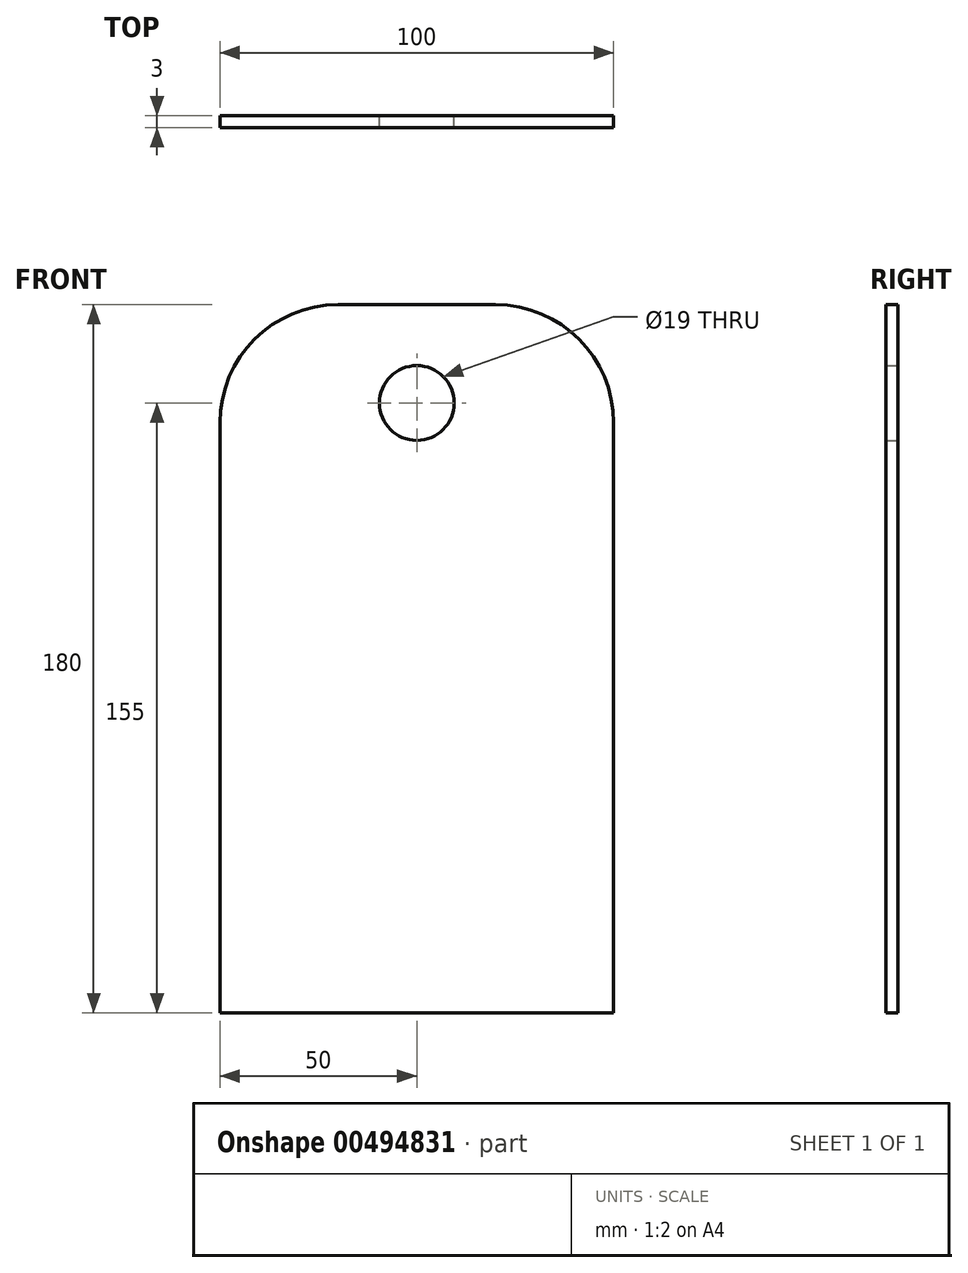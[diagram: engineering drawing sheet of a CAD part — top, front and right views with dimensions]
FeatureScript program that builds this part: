
annotation { "Feature Type Name" : "Feature", "Feature Type Description" : "" }
export const myFeature = defineFeature(function(context is Context, id is Id, definition is map)
    precondition{}
    {
        {
            var Q0;
            Q0=qCreatedBy(makeId("Front.planeOp"),FACE);
            var sketch = newSketch(context, id + "F0", { "sketchPlane" : qUnion([Q0])});
            skLineSegment(sketch, "E0.bottom", {"start": v(50, -90) * mm, "end": v(-50, -90) * mm});
            skLineSegment(sketch, "E0.top", {"start": v(50, 90) * mm, "end": v(-50, 90) * mm});
            skLineSegment(sketch, "E0.left", {"start": v(50, -90) * mm, "end": v(50, 90) * mm});
            skLineSegment(sketch, "E0.right", {"start": v(-50, -90) * mm, "end": v(-50, 90) * mm});
            skPoint(sketch, "E0.middle", {"position": v(0, 0) * mm});
            skCircle(sketch, "E1", {"center": v(0, 65) * mm, "radius": 9.5 * mm});
            skSolve(sketch);
        }
        {
            var Q0;
            Q0 = qSketchRegion(id + "F0", true);
            extrude(context, id + "F1", {"entities" : qUnion([Q0]), "depth" : 3 * mm});
        }
        {
            var Q0;
            Q0=makeQuery(id+"F1.opExtrude","SWEPT_EDGE",EDGE,{"disambiguationData":[OSD([sQuery(id+"F0.wireOp",EDGE,"E0.top"),sQuery(id+"F0.wireOp",EDGE,"E0.right")])]});
            var Q1;
            Q1=makeQuery(id+"F1.opExtrude","SWEPT_EDGE",EDGE,{"disambiguationData":[OSD([sQuery(id+"F0.wireOp",EDGE,"E0.top"),sQuery(id+"F0.wireOp",EDGE,"E0.left")])]});
            fillet(context, id + "F2", {"entities" : qUnion([Q0, Q1]), "radius" : 30 * mm, "tangentPropagation" : true, "allowEdgeOverflow" : false});
        }
    });
